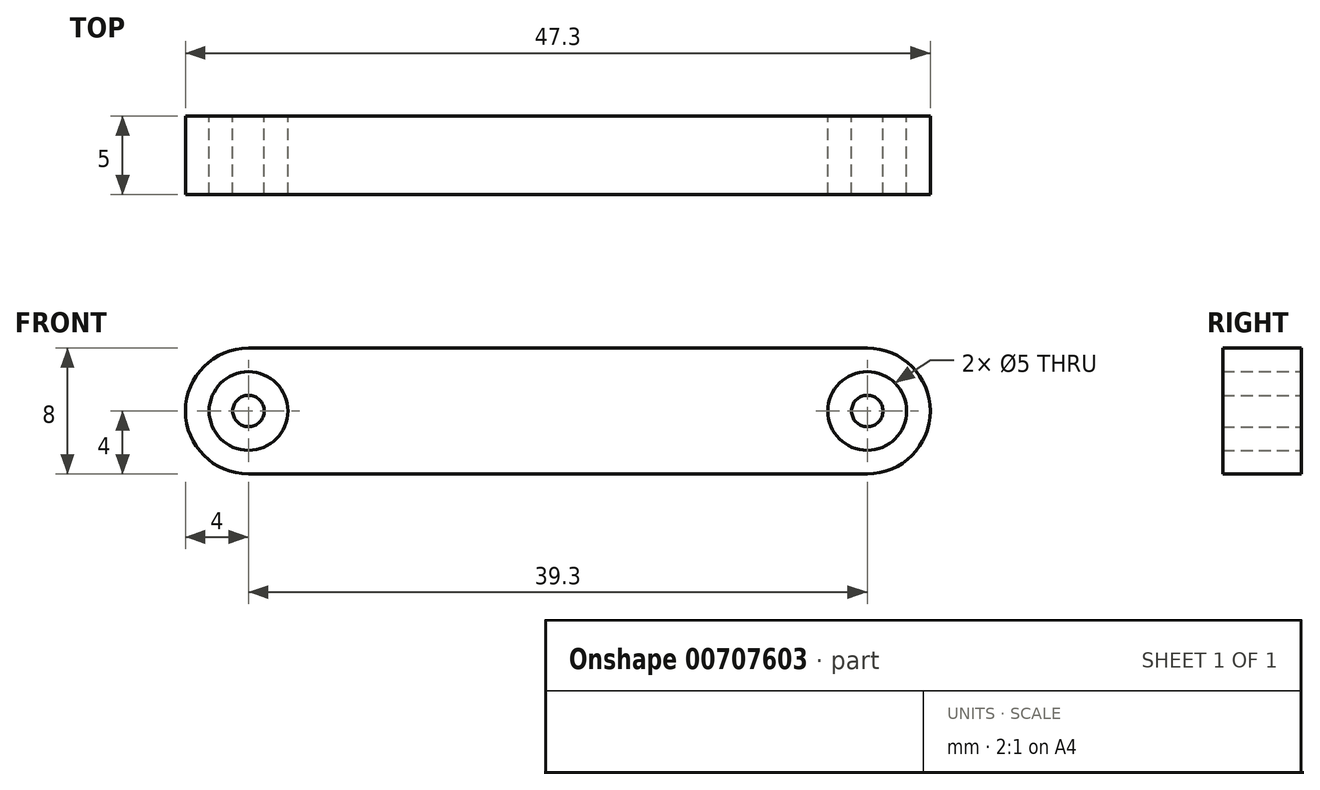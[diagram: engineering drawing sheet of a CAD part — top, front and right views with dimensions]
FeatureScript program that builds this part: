
annotation { "Feature Type Name" : "Feature", "Feature Type Description" : "" }
export const myFeature = defineFeature(function(context is Context, id is Id, definition is map)
    precondition{}
    {
        {
            var Q0;
            Q0=qCreatedBy(makeId("Front.planeOp"),FACE);
            var sketch = newSketch(context, id + "F0", { "sketchPlane" : qUnion([Q0])});
            skCircle(sketch, "E0", {"center": v(0, 0) * mm, "radius": 2.5 * mm});
            skArc(sketch, "E1", {"start": v(0, 4) * mm, "mid": v(-4, 0) * mm, "end": v(0, -4) * mm});
            skCircle(sketch, "E2", {"center": v(0, 0) * mm, "radius": 1 * mm});
            skLineSegment(sketch, "E3", {"start": v(0, 0) * mm, "end": v(39.3, 0) * mm});
            skCircle(sketch, "E4", {"center": v(39.3, 0) * mm, "radius": 1 * mm});
            skArc(sketch, "E5", {"start": v(39.3, -4) * mm, "mid": v(43.3, 0) * mm, "end": v(39.3, 4) * mm});
            skCircle(sketch, "E6", {"center": v(39.3, 0) * mm, "radius": 2.5 * mm});
            skLineSegment(sketch, "E7", {"start": v(0, -4) * mm, "end": v(39.3, -4) * mm});
            skLineSegment(sketch, "E8", {"start": v(0, 4) * mm, "end": v(39.3, 4) * mm});
            skSolve(sketch);
        }
        {
            var Q0;
            Q0=makeQuery(id+"F0.imprint","IMPRINT",FACE,{"disambiguationData":[TD([[makeQuery(id+"F0.imprint","IMPRINT",EDGE,{"derivedFrom":sQuery(id+"F0.wireOp",EDGE,"E2")}),1.0]])]});
            var Q1;
            Q1=makeQuery(id+"F0.imprint","IMPRINT",FACE,{"disambiguationData":[TD([[makeQuery(id+"F0.imprint","IMPRINT",EDGE,{"derivedFrom":sQuery(id+"F0.wireOp",EDGE,"E0")}),-1.0]])]});
            var Q2;
            Q2=makeQuery(id+"F0.imprint","IMPRINT",FACE,{"disambiguationData":[TD([[makeQuery(id+"F0.imprint","IMPRINT",EDGE,{"derivedFrom":sQuery(id+"F0.wireOp",EDGE,"E4")}),1.0]])]});
            extrude(context, id + "F1", {"entities" : qUnion([Q0, Q1, Q2]), "depth" : 5 * mm, "offsetDistance" : 25.4 * mm});
        }
    });
